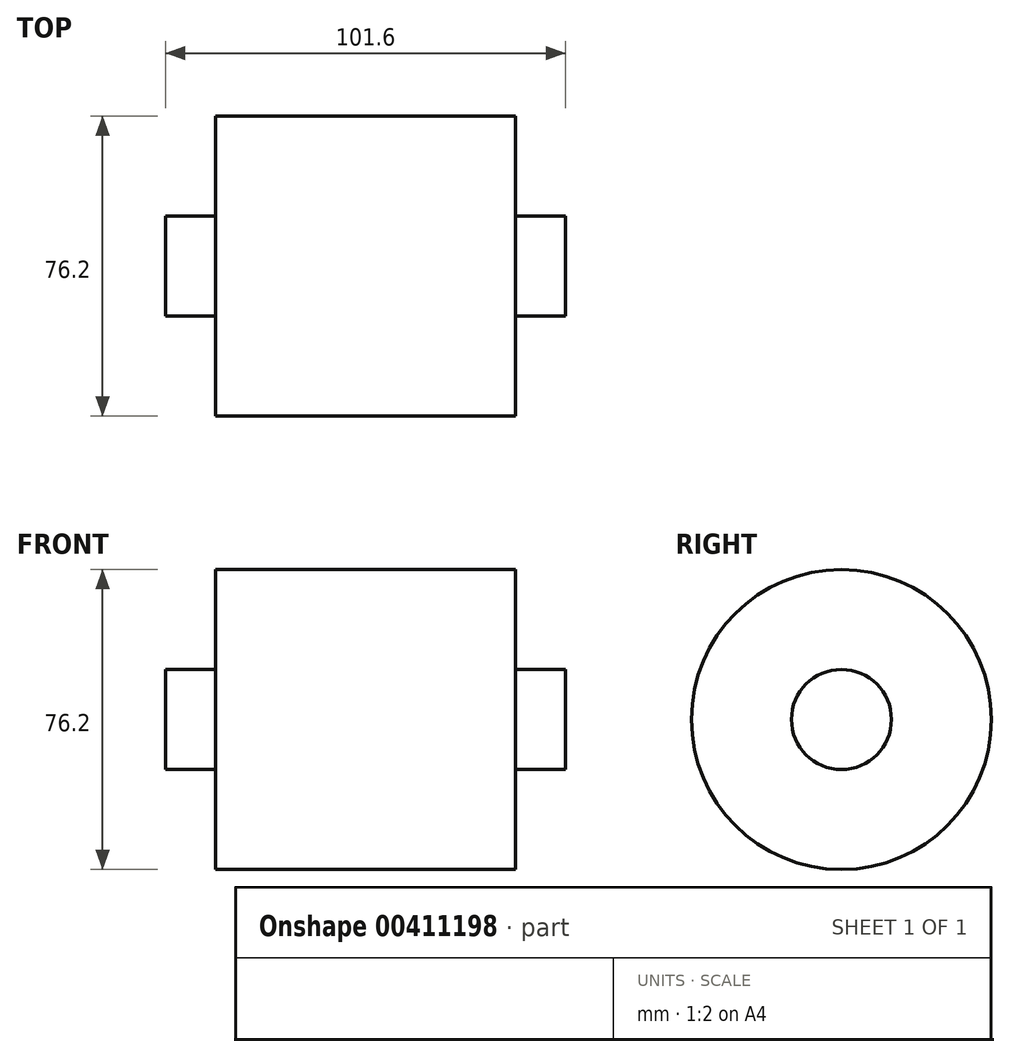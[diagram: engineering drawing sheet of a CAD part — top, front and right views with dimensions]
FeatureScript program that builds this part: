
annotation { "Feature Type Name" : "Feature", "Feature Type Description" : "" }
export const myFeature = defineFeature(function(context is Context, id is Id, definition is map)
    precondition{}
    {
        {
            var Q0;
            Q0=qCreatedBy(makeId("Right.planeOp"),FACE);
            var sketch = newSketch(context, id + "F0", { "sketchPlane" : qUnion([Q0])});
            skCircle(sketch, "E0", {"center": v(0, 0) * mm, "radius": 38.1 * mm});
            skSolve(sketch);
        }
        {
            var Q0;
            Q0 = qSketchRegion(id + "F0", true);
            extrude(context, id + "F1", {"entities" : qUnion([Q0]), "depth" : 76.2 * mm});
        }
        {
            var Q0;
            Q0=makeQuery(id+"F1.opExtrude","CAP_FACE",FACE,{"disambiguationData":[OSD([sQuery(id+"F0.wireOp",EDGE,"E0")])],"isStart":false});
            var sketch = newSketch(context, id + "F2", { "sketchPlane" : qUnion([Q0])});
            skCircle(sketch, "E1", {"center": v(0, 0) * mm, "radius": 12.7 * mm});
            skSolve(sketch);
        }
        {
            var Q0;
            Q0=makeQuery(id+"F2.imprint","IMPRINT",FACE,{"disambiguationData":[TD([[makeQuery(id+"F2.imprint","IMPRINT",EDGE,{"derivedFrom":sQuery(id+"F2.wireOp",EDGE,"E1")}),1.0]])]});
            extrude(context, id + "F3", {"entities" : qUnion([Q0]), "operationType" : NewBodyOperationType.ADD, "depth" : 12.7 * mm});
        }
        {
            var Q0;
            Q0=makeQuery(id+"F1.opExtrude","CAP_FACE",FACE,{"disambiguationData":[OSD([sQuery(id+"F0.wireOp",EDGE,"E0")])],"isStart":true});
            var sketch = newSketch(context, id + "F4", { "sketchPlane" : qUnion([Q0])});
            skCircle(sketch, "E2", {"center": v(0, 0) * mm, "radius": 12.7 * mm});
            skSolve(sketch);
        }
        {
            var Q0;
            Q0 = qSketchRegion(id + "F4", true);
            extrude(context, id + "F5", {"entities" : qUnion([Q0]), "operationType" : NewBodyOperationType.ADD, "depth" : 12.7 * mm});
        }
    });
